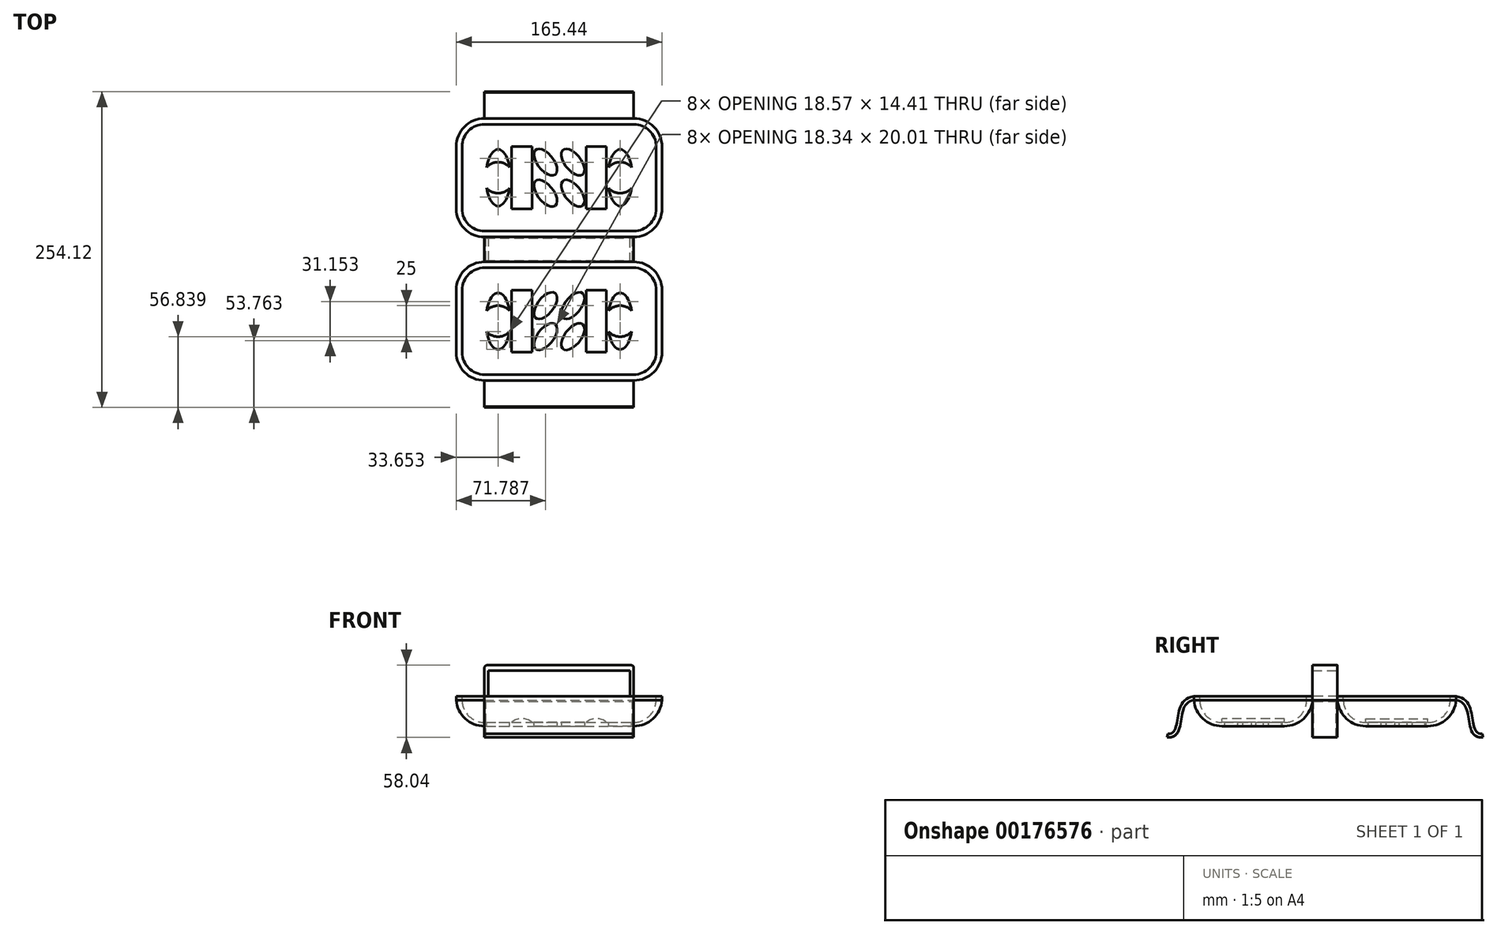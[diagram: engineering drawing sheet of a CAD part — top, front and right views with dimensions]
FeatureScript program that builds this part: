
annotation { "Feature Type Name" : "Feature", "Feature Type Description" : "" }
export const myFeature = defineFeature(function(context is Context, id is Id, definition is map)
    precondition{}
    {
        {
            var Q0;
            Q0=qCreatedBy(makeId("Front.planeOp"),FACE);
            var sketch = newSketch(context, id + "F0", { "sketchPlane" : qUnion([Q0])});
            skLineSegment(sketch, "E0", {"start": v(-60, 0) * mm, "end": v(-38.13, 0) * mm});
            skLineSegment(sketch, "E1", {"start": v(0, 0) * mm, "end": v(21.87, 0) * mm});
            skLineSegment(sketch, "E2", {"start": v(60, 0) * mm, "end": v(60, 18) * mm});
            skArc(sketch, "E3", {"start": v(-60, 0) * mm, "mid": v(-72.72, 5.27) * mm, "end": v(-77.99, 18) * mm});
            skLineSegment(sketch, "E4.0", {"start": v(0, -3) * mm, "end": v(60, -3) * mm});
            skLineSegment(sketch, "E4.1", {"start": v(-60, -3) * mm, "end": v(0, -3) * mm});
            skArc(sketch, "E5", {"start": v(-60, -3) * mm, "mid": v(-75.47, 3.05) * mm, "end": v(-82.72, 17.99) * mm});
            skArc(sketch, "E6.MirrorCS", {"start": v(60, 0) * mm, "mid": v(72.72, 5.27) * mm, "end": v(77.99, 18) * mm});
            skArc(sketch, "E7.MirrorCS", {"start": v(60, -3) * mm, "mid": v(75.47, 3.05) * mm, "end": v(82.72, 17.99) * mm});
            skPoint(sketch, "E8.centerSnap0", {"position": v(-30, -3) * mm});
            skArc(sketch, "E9.trimOffspring", {"start": v(-21.87, 0) * mm, "mid": v(-30, 3.09) * mm, "end": v(-38.13, 0) * mm});
            skLineSegment(sketch, "E10.trimOffspring", {"start": v(-21.87, 0) * mm, "end": v(0, 0) * mm});
            skArc(sketch, "E11.MirrorCS", {"start": v(21.87, 0) * mm, "mid": v(30, 3.09) * mm, "end": v(38.13, 0) * mm});
            skLineSegment(sketch, "E12.trimOffspring", {"start": v(38.13, 0) * mm, "end": v(60, 0) * mm});
            skLineSegment(sketch, "E13", {"start": v(-77.99, 18) * mm, "end": v(-77.99, 20.99) * mm});
            skLineSegment(sketch, "E14", {"start": v(-77.99, 20.99) * mm, "end": v(-82.72, 20.99) * mm});
            skLineSegment(sketch, "E15", {"start": v(-82.72, 20.99) * mm, "end": v(-82.72, 17.99) * mm});
            skLineSegment(sketch, "E16.MirrorCS", {"start": v(77.99, 18) * mm, "end": v(77.99, 20.99) * mm});
            skLineSegment(sketch, "E17.MirrorCS", {"start": v(77.99, 20.99) * mm, "end": v(82.72, 20.99) * mm});
            skLineSegment(sketch, "E18.MirrorCS", {"start": v(82.72, 20.99) * mm, "end": v(82.72, 17.99) * mm});
            skSolve(sketch);
        }
        {
            var Q0;
            Q0=makeQuery(id+"F0.imprint","IMPRINT",FACE,{"disambiguationData":[TD([[makeQuery(id+"F0.imprint","IMPRINT",EDGE,{"derivedFrom":sQuery(id+"F0.wireOp",EDGE,"E0")}),-1.0]])]});
            extrude(context, id + "F1", {"entities" : qUnion([Q0]), "endBound" : BoundingType.SYMMETRIC, "depth" : 50 * mm});
        }
        {
            var Q0;
            Q0=makeQuery(id+"F1.opExtrude","CAP_FACE",FACE,{"disambiguationData":[OSD([sQuery(id+"F0.wireOp",EDGE,"E0"),sQuery(id+"F0.wireOp",EDGE,"E1"),sQuery(id+"F0.wireOp",EDGE,"E3"),sQuery(id+"F0.wireOp",EDGE,"E4.0"),sQuery(id+"F0.wireOp",EDGE,"E4.1"),sQuery(id+"F0.wireOp",EDGE,"E5"),sQuery(id+"F0.wireOp",EDGE,"E6.MirrorCS"),sQuery(id+"F0.wireOp",EDGE,"E7.MirrorCS"),sQuery(id+"F0.wireOp",EDGE,"vXwFxKPh-YDuA-ep5U-sWVK-ZhcQ4KWKkTxs"),sQuery(id+"F0.wireOp",EDGE,"sOCk4LXe-wIjb-z5aJ-w1xU-SIIE50mfUiem"),sQuery(id+"F0.wireOp",EDGE,"E9.trimOffspring"),sQuery(id+"F0.wireOp",EDGE,"E10.trimOffspring"),sQuery(id+"F0.wireOp",EDGE,"E11.MirrorCS"),sQuery(id+"F0.wireOp",EDGE,"E12.trimOffspring")])],"isStart":true});
            var sketch = newSketch(context, id + "F2", { "sketchPlane" : qUnion([Q0])});
            skLineSegment(sketch, "E19", {"start": v(-60, 0) * mm, "end": v(-60, -3) * mm});
            skSolve(sketch);
        }
        {
            var Q0;
            Q0=makeQuery(id+"F2.imprint","IMPRINT",FACE,{"disambiguationData":[TD([[makeQuery(id+"F2.imprint","IMPRINT",EDGE,{"derivedFrom":sQuery(id+"F2.wireOp",EDGE,"E19")}),-1.0]])]});
            var Q1;
            Q1=sQuery(id+"F2.wireOp",EDGE,"E19");
            revolve(context, id + "F3", {"entities" : qUnion([Q0]), "axis" : qUnion([Q1]), "revolveType" : RevolveType.ONE_DIRECTION, "oppositeDirection" : true, "angle" : 90 * degree});
        }
        {
            var Q0;
            Q0=makeQuery(id+"F3.opRevolve","CAP_FACE",FACE,{"disambiguationData":[OSD([sQuery(id+"F0.wireOp",EDGE,"E6.MirrorCS"),sQuery(id+"F0.wireOp",EDGE,"E7.MirrorCS"),sQuery(id+"F0.wireOp",EDGE,"sOCk4LXe-wIjb-z5aJ-w1xU-SIIE50mfUiem"),sQuery(id+"F2.wireOp",EDGE,"E19")])],"isStart":false});
            extrude(context, id + "F4", {"entities" : qUnion([Q0]), "depth" : 120 * mm});
        }
        {
            var Q0;
            Q0=makeQuery(id+"F3.opRevolve","SWEPT_BODY",BODY,{"disambiguationData":[OSD([sQuery(id+"F0.wireOp",EDGE,"E6.MirrorCS"),sQuery(id+"F0.wireOp",EDGE,"E7.MirrorCS"),sQuery(id+"F0.wireOp",EDGE,"sOCk4LXe-wIjb-z5aJ-w1xU-SIIE50mfUiem"),sQuery(id+"F2.wireOp",EDGE,"E19")])]});
            var Q1;
            Q1=qCreatedBy(makeId("Right.planeOp"),FACE);
            mirror(context, id + "F5", {"entities" : qUnion([Q0]), "mirrorPlane" : qUnion([Q1])});
        }
        {
            var Q0;
            Q0=makeQuery(id+"F5.opPattern","COPY",BODY,{"derivedFrom":makeQuery(id+"F3.opRevolve","SWEPT_BODY",BODY,{"disambiguationData":[OSD([sQuery(id+"F0.wireOp",EDGE,"E6.MirrorCS"),sQuery(id+"F0.wireOp",EDGE,"E7.MirrorCS"),sQuery(id+"F0.wireOp",EDGE,"sOCk4LXe-wIjb-z5aJ-w1xU-SIIE50mfUiem"),sQuery(id+"F2.wireOp",EDGE,"E19")])]}),"instanceName":"1"});
            var Q1;
            Q1=makeQuery(id+"F3.opRevolve","SWEPT_BODY",BODY,{"disambiguationData":[OSD([sQuery(id+"F0.wireOp",EDGE,"E6.MirrorCS"),sQuery(id+"F0.wireOp",EDGE,"E7.MirrorCS"),sQuery(id+"F0.wireOp",EDGE,"sOCk4LXe-wIjb-z5aJ-w1xU-SIIE50mfUiem"),sQuery(id+"F2.wireOp",EDGE,"E19")])]});
            var Q2;
            Q2=makeQuery(id+"F4.opExtrude","SWEPT_BODY",BODY,{"disambiguationData":[OSD([sQuery(id+"F0.wireOp",EDGE,"E6.MirrorCS"),sQuery(id+"F0.wireOp",EDGE,"E7.MirrorCS"),sQuery(id+"F0.wireOp",EDGE,"sOCk4LXe-wIjb-z5aJ-w1xU-SIIE50mfUiem"),sQuery(id+"F2.wireOp",EDGE,"E19")])]});
            var Q3;
            Q3=qCreatedBy(makeId("Front.planeOp"),FACE);
            mirror(context, id + "F6", {"operationType" : NewBodyOperationType.ADD, "entities" : qUnion([Q0, Q1, Q2]), "mirrorPlane" : qUnion([Q3])});
        }
        {
            var Q0;
            Q0=makeQuery(id+"F6.opPattern","COPY",FACE,{"derivedFrom":makeQuery(id+"F4.opExtrude","SWEPT_FACE",FACE,{"disambiguationData":[OSD([sQuery(id+"F0.wireOp",EDGE,"E18.MirrorCS")])]}),"instanceName":"1"});
            extrude(context, id + "F7", {"entities" : qUnion([Q0]), "depth" : 10 * mm});
        }
        {
            var Q0;
            Q0=makeQuery(id+"F1.opExtrude","SWEPT_FACE",FACE,{"disambiguationData":[OSD([sQuery(id+"F0.wireOp",EDGE,"E1"),sQuery(id+"F0.wireOp",EDGE,"E10.trimOffspring")])]});
            var sketch = newSketch(context, id + "F8", { "sketchPlane" : qUnion([Q0])});
            skLineSegment(sketch, "E20", {"start": v(21.87, 25) * mm, "end": v(0, 25) * mm});
            skLineSegment(sketch, "E21", {"start": v(0, 25) * mm, "end": v(-21.87, 25) * mm});
            skLineSegment(sketch, "E22", {"start": v(-21.87, 25) * mm, "end": v(-21.87, 0) * mm});
            skLineSegment(sketch, "E23", {"start": v(-21.87, 0) * mm, "end": v(-21.87, -25) * mm});
            skLineSegment(sketch, "E24", {"start": v(-21.87, -25) * mm, "end": v(0, -25) * mm});
            skLineSegment(sketch, "E25", {"start": v(0, -25) * mm, "end": v(21.87, -25) * mm});
            skLineSegment(sketch, "E26", {"start": v(21.87, -25) * mm, "end": v(21.87, 0) * mm});
            skLineSegment(sketch, "E27", {"start": v(21.87, 0) * mm, "end": v(21.87, 25) * mm});
            skEllipse(sketch, "E28", {"center": v(-10.93, 12.5) * mm, "majorRadius": 12.72 * mm, "minorRadius": 6.51 * mm, "majorAxis": v(0.62, -0.79)});
            skPoint(sketch, "E28.centerSnap0", {"position": v(-21.87, 12.5) * mm});
            skPoint(sketch, "E28.centerSnap1", {"position": v(-10.93, 25) * mm});
            skEllipse(sketch, "E29.0.1.0", {"center": v(-10.93, -12.5) * mm, "majorRadius": 12.72 * mm, "minorRadius": 6.51 * mm, "majorAxis": v(0.62, -0.79)});
            skEllipse(sketch, "E29.1.0.0", {"center": v(11.07, 12.5) * mm, "majorRadius": 12.72 * mm, "minorRadius": 6.51 * mm, "majorAxis": v(0.62, -0.79)});
            skEllipse(sketch, "E29.1.1.0", {"center": v(11.07, -12.5) * mm, "majorRadius": 12.72 * mm, "minorRadius": 6.51 * mm, "majorAxis": v(0.62, -0.79)});
            skLineSegment(sketch, "E29.direction1", {"start": v(-10.93, 12.5) * mm, "end": v(11.07, 12.5) * mm, "construction": true});
            skLineSegment(sketch, "E29.direction2", {"start": v(-10.93, 12.5) * mm, "end": v(-10.93, -12.5) * mm, "construction": true});
            skLineSegment(sketch, "E30", {"start": v(60, 25) * mm, "end": v(38.13, 25) * mm});
            skLineSegment(sketch, "E31", {"start": v(60, 25) * mm, "end": v(60, -25) * mm});
            skLineSegment(sketch, "E32", {"start": v(60, -25) * mm, "end": v(38.13, -25) * mm});
            skLineSegment(sketch, "E33", {"start": v(38.13, -25) * mm, "end": v(38.13, 25) * mm});
            skPoint(sketch, "E34.centerSnap0", {"position": v(60, 0) * mm});
            skPoint(sketch, "E34.centerSnap1", {"position": v(49.07, 25) * mm});
            skLineSegment(sketch, "E35", {"start": v(0, 25) * mm, "end": v(0, -25) * mm});
            skCircle(sketch, "E36", {"center": v(49.07, 0) * mm, "radius": 12.5 * mm});
            skEllipse(sketch, "E37", {"center": v(49.07, 0) * mm, "majorRadius": 22.78 * mm, "minorRadius": 9.98 * mm, "majorAxis": v(0, -1)});
            skEllipse(sketch, "E38.MirrorC", {"center": v(-49.07, 0) * mm, "majorRadius": 22.78 * mm, "minorRadius": 9.98 * mm, "majorAxis": v(0, -1)});
            skCircle(sketch, "E39.MirrorC", {"center": v(-49.07, 0) * mm, "radius": 12.5 * mm});
            skSolve(sketch);
        }
        {
            var Q0;
            {var subQ0=sQuery(id+"F8.wireOp",EDGE,"E39.MirrorC");var subQ1=sQuery(id+"F8.wireOp",EDGE,"E38.MirrorC");var subQ2=makeQuery(id+"F8.imprint","INTERSECT",VERTEX,{"disambiguationData":[OD(1.0)],"derivedFrom":[subQ1,subQ0]});Q0=makeQuery(id+"F8.imprint","IMPRINT",FACE,{"disambiguationData":[TD([[makeQuery(id+"F8.imprint","IMPRINT",EDGE,{"disambiguationData":[TD([[subQ2,1.0]])],"derivedFrom":subQ1}),1.0]])]});}
            var Q1;
            {var subQ0=sQuery(id+"F8.wireOp",EDGE,"E39.MirrorC");var subQ1=sQuery(id+"F8.wireOp",EDGE,"E38.MirrorC");var subQ2=makeQuery(id+"F8.imprint","INTERSECT",VERTEX,{"disambiguationData":[OD(0.0)],"derivedFrom":[subQ1,subQ0]});Q1=makeQuery(id+"F8.imprint","IMPRINT",FACE,{"disambiguationData":[TD([[makeQuery(id+"F8.imprint","IMPRINT",EDGE,{"disambiguationData":[TD([[subQ2,-1.0]])],"derivedFrom":subQ1}),1.0]])]});}
            var Q2;
            Q2=makeQuery(id+"F8.imprint","IMPRINT",FACE,{"disambiguationData":[TD([[makeQuery(id+"F8.imprint","IMPRINT",EDGE,{"derivedFrom":sQuery(id+"F8.wireOp",EDGE,"E29.0.1.0")}),1.0]])]});
            var Q3;
            Q3=makeQuery(id+"F8.imprint","IMPRINT",FACE,{"disambiguationData":[TD([[makeQuery(id+"F8.imprint","IMPRINT",EDGE,{"derivedFrom":sQuery(id+"F8.wireOp",EDGE,"E28")}),1.0]])]});
            var Q4;
            Q4=makeQuery(id+"F8.imprint","IMPRINT",FACE,{"disambiguationData":[TD([[makeQuery(id+"F8.imprint","IMPRINT",EDGE,{"derivedFrom":sQuery(id+"F8.wireOp",EDGE,"E29.1.1.0")}),1.0]])]});
            var Q5;
            Q5=makeQuery(id+"F8.imprint","IMPRINT",FACE,{"disambiguationData":[TD([[makeQuery(id+"F8.imprint","IMPRINT",EDGE,{"derivedFrom":sQuery(id+"F8.wireOp",EDGE,"E29.1.0.0")}),1.0]])]});
            var Q6;
            {var subQ0=sQuery(id+"F8.wireOp",EDGE,"E37");var subQ1=sQuery(id+"F8.wireOp",EDGE,"E36");var subQ2=makeQuery(id+"F8.imprint","INTERSECT",VERTEX,{"disambiguationData":[OD(2.0)],"derivedFrom":[subQ1,subQ0]});Q6=makeQuery(id+"F8.imprint","IMPRINT",FACE,{"disambiguationData":[TD([[makeQuery(id+"F8.imprint","IMPRINT",EDGE,{"disambiguationData":[TD([[subQ2,-1.0]])],"derivedFrom":subQ1}),-1.0]])]});}
            var Q7;
            {var subQ0=sQuery(id+"F8.wireOp",EDGE,"E37");var subQ1=sQuery(id+"F8.wireOp",EDGE,"E36");var subQ2=makeQuery(id+"F8.imprint","INTERSECT",VERTEX,{"disambiguationData":[OD(0.0)],"derivedFrom":[subQ1,subQ0]});Q7=makeQuery(id+"F8.imprint","IMPRINT",FACE,{"disambiguationData":[TD([[makeQuery(id+"F8.imprint","IMPRINT",EDGE,{"disambiguationData":[TD([[subQ2,-1.0]])],"derivedFrom":subQ1}),-1.0]])]});}
            extrude(context, id + "F9", {"entities" : qUnion([Q0, Q1, Q2, Q3, Q4, Q5, Q6, Q7]), "operationType" : NewBodyOperationType.REMOVE, "endBound" : BoundingType.THROUGH_ALL, "oppositeDirection" : true, "depth" : 25 * mm});
        }
        {
            var Q0;
            Q0=makeQuery(id+"F1.opExtrude","SWEPT_BODY",BODY,{"disambiguationData":[OSD([sQuery(id+"F0.wireOp",EDGE,"E0"),sQuery(id+"F0.wireOp",EDGE,"E1"),sQuery(id+"F0.wireOp",EDGE,"E3"),sQuery(id+"F0.wireOp",EDGE,"E4.0"),sQuery(id+"F0.wireOp",EDGE,"E4.1"),sQuery(id+"F0.wireOp",EDGE,"E5"),sQuery(id+"F0.wireOp",EDGE,"E6.MirrorCS"),sQuery(id+"F0.wireOp",EDGE,"E7.MirrorCS"),sQuery(id+"F0.wireOp",EDGE,"E9.trimOffspring"),sQuery(id+"F0.wireOp",EDGE,"E10.trimOffspring"),sQuery(id+"F0.wireOp",EDGE,"E11.MirrorCS"),sQuery(id+"F0.wireOp",EDGE,"E12.trimOffspring"),sQuery(id+"F0.wireOp",EDGE,"E13"),sQuery(id+"F0.wireOp",EDGE,"E14"),sQuery(id+"F0.wireOp",EDGE,"E15"),sQuery(id+"F0.wireOp",EDGE,"E16.MirrorCS"),sQuery(id+"F0.wireOp",EDGE,"E17.MirrorCS"),sQuery(id+"F0.wireOp",EDGE,"E18.MirrorCS")])]});
            var Q1;
            Q1=makeQuery(id+"F7.opExtrude","SWEPT_BODY",BODY,{"disambiguationData":[OSD([sQuery(id+"F0.wireOp",EDGE,"E18.MirrorCS")])]});
            var Q2;
            Q2=makeQuery(id+"F7.opExtrude","CAP_FACE",FACE,{"disambiguationData":[OSD([sQuery(id+"F0.wireOp",EDGE,"E18.MirrorCS")])],"isStart":false});
            mirror(context, id + "F10", {"entities" : qUnion([Q0, Q1]), "mirrorPlane" : qUnion([Q2])});
        }
        {
            var Q0;
            Q0=qCreatedBy(makeId("Right.planeOp"),FACE);
            var sketch = newSketch(context, id + "F11", { "sketchPlane" : qUnion([Q0])});
            skFitSpline(sketch, "E40", {"points": [v(-163.16, 20.99) * mm, v(-184.03, -9.01) * mm], "startDerivative": vector(-57.52, -7.6) * mm, "endDerivative": vector(-37.75, 4.6) * mm});
            skSolve(sketch);
        }
        {
            var Q0;
            Q0=makeQuery(id+"F10.opPattern","COPY",FACE,{"derivedFrom":makeQuery(id+"F4.opExtrude","SWEPT_FACE",FACE,{"disambiguationData":[OSD([sQuery(id+"F0.wireOp",EDGE,"E18.MirrorCS")])]}),"instanceName":"1"});
            var Q1;
            Q1=sQuery(id+"F11.wireOp",EDGE,"E40");
            sweep(context, id + "F12", {"profiles" : qUnion([Q0]), "path" : qUnion([Q1])});
        }
        {
            var Q0;
            Q0=makeQuery(id+"F7.opExtrude","CAP_EDGE",EDGE,{"disambiguationData":[OSD([sQuery(id+"F0.wireOp",EDGE,"E17.MirrorCS"),sQuery(id+"F0.wireOp",EDGE,"E18.MirrorCS")])],"isStart":false});
            cPoint(context, id + "F13", {"entities" : qUnion([Q0]), "parameter" : 0.5});
        }
        {
            var Q0;
            Q0=qCreatedBy(makeId("Front.planeOp"),FACE);
            var Q1;
            Q1 = qCreatedBy(id + "F13" ,VERTEX);
            cPlane(context, id + "F14", {"entities" : qUnion([Q0, Q1]), "cplaneType" : CPlaneType.PLANE_POINT, "offset" : 25 * mm, "width" : 150 * mm, "height" : 150 * mm});
        }
        {
            var Q0;
            Q0=makeQuery(id+"F12.opSweep","SWEPT_BODY",BODY,{"disambiguationData":[OSD([sQuery(id+"F0.wireOp",EDGE,"E18.MirrorCS"),sQuery(id+"F11.wireOp",EDGE,"E40")])]});
            var Q1;
            Q1=qCreatedBy(id+"F14.planeOp",FACE);
            mirror(context, id + "F15", {"operationType" : NewBodyOperationType.ADD, "entities" : qUnion([Q0]), "mirrorPlane" : qUnion([Q1])});
        }
        {
            var Q0;
            Q0=makeQuery(id+"F7.opExtrude","SWEPT_FACE",FACE,{"disambiguationData":[OSD([sQuery(id+"F0.wireOp",EDGE,"E17.MirrorCS"),sQuery(id+"F0.wireOp",EDGE,"E18.MirrorCS")])]});
            var sketch = newSketch(context, id + "F16", { "sketchPlane" : qUnion([Q0])});
            skLineSegment(sketch, "E41", {"start": v(-60, -57.72) * mm, "end": v(-60, -67.72) * mm});
            skLineSegment(sketch, "E42", {"start": v(-60, -57.72) * mm, "end": v(-60, -47.72) * mm});
            skLineSegment(sketch, "E43", {"start": v(-60, -47.72) * mm, "end": v(-57, -47.72) * mm});
            skLineSegment(sketch, "E44", {"start": v(-57, -47.72) * mm, "end": v(-57, -67.72) * mm});
            skLineSegment(sketch, "E45", {"start": v(-57, -67.72) * mm, "end": v(-60, -67.72) * mm});
            skSolve(sketch);
        }
        {
            var Q0;
            {var subQ0=sQuery(id+"F16.wireOp",EDGE,"E41");Q0=makeQuery(id+"F16.imprint","IMPRINT",FACE,{"disambiguationData":[TD([[makeQuery(id+"F16.imprint","IMPRINT",EDGE,{"derivedFrom":subQ0}),1.0]])]});}
            var Q1;
            {var subQ0=sQuery(id+"F16.wireOp",EDGE,"E42");Q1=makeQuery(id+"F16.imprint","IMPRINT",FACE,{"disambiguationData":[TD([[makeQuery(id+"F16.imprint","IMPRINT",EDGE,{"derivedFrom":subQ0}),-1.0]])]});}
            extrude(context, id + "F17", {"entities" : qUnion([Q0, Q1]), "depth" : 25 * mm});
        }
        {
            var Q0;
            Q0=makeQuery(id+"F17.opExtrude","SWEPT_BODY",BODY,{"disambiguationData":[OSD([sQuery(id+"F16.wireOp",EDGE,"E41"),sQuery(id+"F16.wireOp",EDGE,"E42"),sQuery(id+"F16.wireOp",EDGE,"E43"),sQuery(id+"F16.wireOp",EDGE,"E44"),sQuery(id+"F16.wireOp",EDGE,"E45")])]});
            var Q1;
            Q1=qCreatedBy(makeId("Right.planeOp"),FACE);
            mirror(context, id + "F18", {"operationType" : NewBodyOperationType.ADD, "entities" : qUnion([Q0]), "mirrorPlane" : qUnion([Q1])});
        }
        {
            var Q0;
            Q0=makeQuery(id+"F17.opExtrude","SWEPT_FACE",FACE,{"disambiguationData":[OSD([sQuery(id+"F16.wireOp",EDGE,"E44")])]});
            var sketch = newSketch(context, id + "F19", { "sketchPlane" : qUnion([Q0])});
            skLineSegment(sketch, "E46", {"start": v(-67.72, 45.99) * mm, "end": v(-67.72, 41.75) * mm});
            skLineSegment(sketch, "E47", {"start": v(-67.72, 41.75) * mm, "end": v(-47.72, 41.75) * mm});
            skLineSegment(sketch, "E48", {"start": v(-47.72, 41.75) * mm, "end": v(-47.72, 45.99) * mm});
            skLineSegment(sketch, "E49", {"start": v(-47.72, 45.99) * mm, "end": v(-67.72, 45.99) * mm});
            skSolve(sketch);
        }
        {
            var Q0;
            Q0=makeQuery(id+"F19.imprint","IMPRINT",FACE,{"disambiguationData":[TD([[makeQuery(id+"F19.imprint","IMPRINT",EDGE,{"derivedFrom":sQuery(id+"F19.wireOp",EDGE,"E46")}),1.0]])]});
            extrude(context, id + "F20", {"entities" : qUnion([Q0]), "operationType" : NewBodyOperationType.ADD, "depth" : 114 * mm});
        }
        {
            var Q0;
            Q0=makeQuery(id+"F17.opExtrude","CAP_EDGE",EDGE,{"disambiguationData":[OSD([sQuery(id+"F16.wireOp",EDGE,"E41"),sQuery(id+"F16.wireOp",EDGE,"E42")])],"isStart":false});
            var Q1;
            Q1=makeQuery(id+"F20.opExtrude","CAP_EDGE",EDGE,{"disambiguationData":[OSD([sQuery(id+"F19.wireOp",EDGE,"E47")])],"isStart":true});
            var Q2;
            Q2=makeQuery(id+"F18.opPattern","COPY",EDGE,{"derivedFrom":makeQuery(id+"F17.opExtrude","CAP_EDGE",EDGE,{"disambiguationData":[OSD([sQuery(id+"F16.wireOp",EDGE,"E41"),sQuery(id+"F16.wireOp",EDGE,"E42")])],"isStart":false}),"instanceName":"1"});
            var Q3;
            Q3=makeQuery(id+"F20.opExtrude","CAP_EDGE",EDGE,{"disambiguationData":[OSD([sQuery(id+"F19.wireOp",EDGE,"E47")])],"isStart":false});
            fillet(context, id + "F21", {"entities" : qUnion([Q0, Q1, Q2, Q3]), "radius" : 2 * mm, "tangentPropagation" : true, "allowEdgeOverflow" : false});
        }
        {
            var Q0;
            Q0=makeQuery(id+"F10.opPattern","COPY",FACE,{"derivedFrom":makeQuery(id+"F7.opExtrude","SWEPT_FACE",FACE,{"disambiguationData":[OSD([sQuery(id+"F0.wireOp",EDGE,"E7.MirrorCS"),sQuery(id+"F0.wireOp",EDGE,"E18.MirrorCS")])]}),"instanceName":"1"});
            var Q1;
            Q1=makeQuery(id+"F7.opExtrude","SWEPT_FACE",FACE,{"disambiguationData":[OSD([sQuery(id+"F0.wireOp",EDGE,"E7.MirrorCS"),sQuery(id+"F0.wireOp",EDGE,"E18.MirrorCS")])]});
            extrude(context, id + "F22", {"entities" : qUnion([Q0, Q1]), "depth" : 30 * mm});
        }
        {
            var Q0;
            {var subQ0=sQuery(id+"F0.wireOp",EDGE,"E18.MirrorCS");var subQ1=sQuery(id+"F0.wireOp",EDGE,"E7.MirrorCS");Q0=makeQuery(id+"F22.opExtrude","CAP_FACE",FACE,{"disambiguationData":[OSD([subQ1,subQ0]),TDD([makeQuery(id+"F7.opExtrude","SWEPT_FACE",FACE,{"disambiguationData":[OSD([subQ1,subQ0])]})])],"isStart":false});}
            var Q1;
            {var subQ0=sQuery(id+"F0.wireOp",EDGE,"E18.MirrorCS");var subQ1=sQuery(id+"F0.wireOp",EDGE,"E7.MirrorCS");Q1=makeQuery(id+"F22.opExtrude","CAP_FACE",FACE,{"disambiguationData":[OSD([subQ1,subQ0]),TDD([makeQuery(id+"F10.opPattern","COPY",FACE,{"derivedFrom":makeQuery(id+"F7.opExtrude","SWEPT_FACE",FACE,{"disambiguationData":[OSD([subQ1,subQ0])]}),"instanceName":"1"})])],"isStart":false});}
            shell(context, id + "F23", {"entities" : qUnion([Q0, Q1]), "thickness" : 1 * mm});
        }
    });
